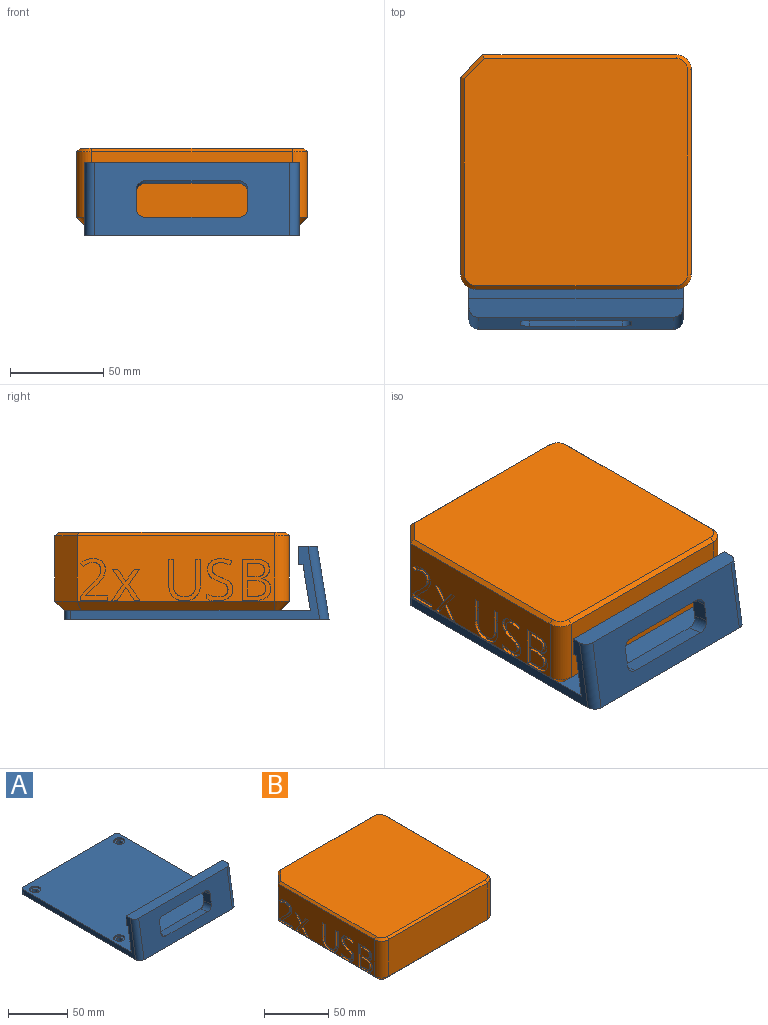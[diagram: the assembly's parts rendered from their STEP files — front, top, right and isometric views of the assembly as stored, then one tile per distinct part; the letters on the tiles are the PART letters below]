
ASSEMBLY  parts=2 mates=1
PART A: 34 faces, bbox 115x142x41.1 mm
  f0: plane 115x24.41mm, normal (0,0.99,-0.16), area 1665.7mm2, adj f4,f5,f8,f9,f22,f23,f24,f25
  f1: plane 105x39.49mm, normal (0,-0.99,0.16), area 3022.2mm2, adj f2,f7,f22,f23,f24,f25,f26,f27
  f2: plane 142x115mm, normal (0,0,-1), area 16234.2mm2, adj f1,f3,f8,f9,f10,f13,f16,f19
  f3: plane 109x5.08mm, normal (0,1,0), area 553.7mm2, adj f2,f4,f30,f31
  f4: plane 131.92x115mm, normal (0,0,1), area 14882.1mm2, adj f0,f3,f8,f9,f12,f15,f18,f21
  f5: plane 115x2.35mm, normal (0,0,-1), area 269.8mm2, adj f0,f6,f8,f9
  f6: plane 115x10mm, normal (0,1,0), area 1150mm2, adj f5,f7,f8,f9
  f7: plane 115x10mm, normal (0,0,1), area 1139.1mm2, adj f1,f6,f8,f9,f32,f33
  f8: plane 133.94x39.49mm, normal (1,0,0), area 838.2mm2, adj f0,f2,f4,f5,f6,f7,f31,f33
  f9: plane 133.94x39.49mm, normal (-1,0,0), area 838.2mm2, adj f0,f2,f4,f5,f6,f7,f30,f32
  f10: cylinder r=2.54mm len=5.08mm, axis (0,0,1), area 56.8mm2, adj f2,f11
  f11: plane 9.53x9.53mm, normal (0,0,1), area 51mm2, adj f10,f12
  f12: cylinder r=4.76mm len=9.53mm, axis (0,0,1), area 45.6mm2, adj f4,f11
  f13: cylinder r=2.54mm len=5.08mm, axis (0,0,1), area 56.8mm2, adj f2,f14
  f14: plane 9.53x9.53mm, normal (0,0,1), area 51mm2, adj f13,f15
  f15: cylinder r=4.76mm len=9.53mm, axis (0,0,1), area 45.6mm2, adj f4,f14
  f16: cylinder r=2.54mm len=5.08mm, axis (0,0,1), area 56.8mm2, adj f2,f17
  f17: plane 9.53x9.53mm, normal (0,0,1), area 51mm2, adj f16,f18
  f18: cylinder r=4.76mm len=9.53mm, axis (0,0,1), area 45.6mm2, adj f4,f17
  f19: cylinder r=2.54mm len=5.08mm, axis (0,0,1), area 56.8mm2, adj f2,f20
  f20: plane 9.53x9.53mm, normal (0,0,1), area 51mm2, adj f19,f21
  f21: cylinder r=4.76mm len=9.53mm, axis (0,0,1), area 45.6mm2, adj f4,f20
  f22: plane 11.17x10.59mm, normal (-1,0,0), area 90mm2, adj f0,f1,f26,f29
  f23: plane 49.84x9.03mm, normal (0,-0.16,-0.99), area 455.7mm2, adj f0,f1,f26,f27
  f24: plane 11.17x10.59mm, normal (1,0,0), area 90mm2, adj f0,f1,f27,f28
  f25: plane 49.84x9.03mm, normal (0,0.16,0.99), area 455.7mm2, adj f0,f1,f28,f29
  f26: cylinder r=5.08mm len=9.83mm, axis (0,-0.99,0.16), area 73mm2, adj f0,f1,f22,f23
  f27: cylinder r=5.08mm len=9.83mm, axis (0,0.99,-0.16), area 73mm2, adj f0,f1,f23,f24
  f28: cylinder r=5.08mm len=9.83mm, axis (0,-0.99,0.16), area 73mm2, adj f0,f1,f24,f25
  f29: cylinder r=5.08mm len=9.83mm, axis (0,0.99,-0.16), area 73mm2, adj f0,f1,f22,f25
  f30: cylinder r=3mm len=5.08mm, axis (0,0,1), area 23.9mm2, adj f2,f3,f4,f9
  f31: cylinder r=3mm len=5.08mm, axis (0,0,-1), area 23.9mm2, adj f2,f3,f4,f8
  f32: cylinder r=5mm len=41.08mm, axis (0,-0.16,-0.99), area 314.2mm2, adj f1,f2,f7,f9
  f33: cylinder r=5mm len=41.08mm, axis (0,0.16,0.99), area 314.2mm2, adj f1,f2,f7,f8
PART B: 268 faces, bbox 124x126x46.3 mm
  f0: plane 110x35mm, normal (1,0,0), area 3184.7mm2, adj f6,f8,f10,f121,f122,f123,f124,f125
  f1: plane 106x35mm, normal (-1,0,0), area 2969.8mm2, adj f7,f9,f17,f18,f19,f20,f27,f28
  f2: plane 104x35mm, normal (0,1,0), area 3640mm2, adj f6,f9,f13,f263
  f3: plane 108x35mm, normal (0,-1,0), area 3780mm2, adj f7,f8,f14,f264
  f4: plane 122x120mm, normal (0,0,1), area 14558.2mm2, adj f260,f261,f262,f263,f264,f265,f266,f267
  f5: plane 116x114mm, normal (0,0,-1), area 13152.7mm2, adj f10,f11,f12,f13,f14,f15,f16,f17
  f6: cylinder r=8mm len=35mm, axis (0,0,1), area 439.8mm2, adj f0,f2,f11,f261
  f7: cylinder r=8mm len=35mm, axis (0,0,1), area 439.8mm2, adj f1,f3,f16,f266
  f8: cylinder r=8mm len=35mm, axis (0,0,-1), area 439.8mm2, adj f0,f3,f12,f262
  f9: plane 35x12mm, normal (-0.71,0.71,0), area 594mm2, adj f1,f2,f15,f265
  f10: plane 110x5mm, normal (0.71,0,-0.71), area 777.8mm2, adj f0,f5,f11,f12
  f11: cone r=3mm half-angle=45deg, axis (0,0,1), area 61.1mm2, adj f5,f6,f10,f13
  f12: cone r=3mm half-angle=45deg, axis (0,0,1), area 61.1mm2, adj f5,f8,f10,f14
  f13: plane 104x5mm, normal (0,0.71,-0.71), area 728.1mm2, adj f2,f5,f11,f15
  f14: plane 108x5mm, normal (0,-0.71,-0.71), area 763.7mm2, adj f3,f5,f12,f16
  f15: plane 14.07x14.07mm, normal (-0.5,0.5,-0.71), area 105.4mm2, adj f5,f9,f13,f17
  f16: cone r=3mm half-angle=45deg, axis (0,0,1), area 61.1mm2, adj f5,f7,f14,f17
  f17: plane 106x5mm, normal (-0.71,0,-0.71), area 742.2mm2, adj f1,f5,f15,f16
  f18: plane 1.52x0.15mm, normal (0,1,0), area 0.2mm2, adj f1,f30,f31,f43
  f19: plane 6.25x1.52mm, normal (0,0,-1), area 9.5mm2, adj f1,f20,f34,f43
  f20: plane 22.11x1.52mm, normal (0,-1,0), area 33.7mm2, adj f1,f19,f27,f43
  f21: plane 4.23x1.52mm, normal (0,0,-1), area 6.5mm2, adj f22,f38,f43,f44
  f22: plane 7.24x1.52mm, normal (0,1,0), area 11mm2, adj f21,f26,f43,f44
  f23: plane 4.62x1.52mm, normal (0,0,-1), area 7mm2, adj f24,f41,f43,f45
  f24: plane 8.27x1.52mm, normal (0,1,0), area 12.6mm2, adj f23,f25,f43,f45
  f25: plane 4.4x1.52mm, normal (0,0,1), area 6.7mm2, adj f24,f42,f43,f45
  f26: plane 3.78x1.52mm, normal (0,0,1), area 5.8mm2, adj f22,f35,f43,f44
  f27: plane 7.71x1.52mm, normal (0,0,1), area 11.8mm2, adj f1,f20,f28,f43
  f28: extruded ~5.6x1.66mm, area 9.1mm2, adj f1,f27,f29,f43
  f29: extruded ~4.63x2mm, area 8mm2, adj f1,f28,f30,f43
  f30: extruded ~5.29x5.04mm, area 12.3mm2, adj f1,f18,f29,f43
  f31: extruded ~3.2x1.66mm, area 5.6mm2, adj f1,f18,f32,f43
  f32: extruded ~3.25x1.52mm, area 5.3mm2, adj f1,f31,f33,f43
  f33: extruded ~4.16x1.97mm, area 7.3mm2, adj f1,f32,f34,f43
  f34: extruded ~6.37x1.52mm, area 10mm2, adj f1,f19,f33,f43
  f35: extruded ~4.23x1.52mm, area 6.6mm2, adj f26,f36,f43,f44
  f36: extruded ~2.69x1.52mm, area 4.8mm2, adj f35,f37,f43,f44
  f37: extruded ~2.88x1.52mm, area 4.9mm2, adj f36,f38,f43,f44
  f38: extruded ~3.92x1.52mm, area 6.2mm2, adj f21,f37,f43,f44
  f39: extruded ~3.02x1.52mm, area 5.3mm2, adj f40,f42,f43,f45
  f40: extruded ~3.25x1.52mm, area 5.6mm2, adj f39,f41,f43,f45
  f41: extruded ~4.03x1.52mm, area 6.4mm2, adj f23,f40,f43,f45
  f42: extruded ~4.21x1.52mm, area 6.7mm2, adj f25,f39,f43,f45
  f43: plane 22.11x15.32mm, normal (-1,0,0), area 166.7mm2, adj f18,f19,f20,f21,f22,f23,f24,f25
  f44: plane 9.35x7.24mm, normal (-1,0,0), area 61.8mm2, adj f21,f22,f26,f35,f36,f37,f38
  f45: plane 10x8.27mm, normal (-1,0,0), area 75.4mm2, adj f23,f24,f25,f39,f40,f41,f42
  f46: plane 2.24x1.52mm, normal (0,0.94,0.34), area 3.6mm2, adj f1,f53,f54,f71
  f47: plane 2.48x1.52mm, normal (0,-1,0), area 3.8mm2, adj f1,f65,f66,f71
  f48: extruded ~3.08x1.52mm, area 5.1mm2, adj f1,f49,f70,f71
  f49: extruded ~1.52x1.43mm, area 3mm2, adj f1,f48,f50,f71
  f50: extruded ~1.88x1.52mm, area 3mm2, adj f1,f49,f51,f71
  f51: extruded ~2.43x1.52mm, area 4.3mm2, adj f1,f50,f52,f71
  f52: extruded ~3.19x1.52mm, area 5.1mm2, adj f1,f51,f53,f71
  f53: extruded ~5.32x1.52mm, area 8.4mm2, adj f1,f46,f52,f71
  f54: extruded ~6.06x1.52mm, area 9.5mm2, adj f1,f46,f55,f71
  f55: extruded ~5.08x1.52mm, area 8.2mm2, adj f1,f54,f56,f71
  f56: extruded ~4.07x1.92mm, area 7.1mm2, adj f1,f55,f57,f71
  f57: extruded ~3.95x1.52mm, area 6.5mm2, adj f1,f56,f58,f71
  f58: extruded ~4.41x2.62mm, area 7.9mm2, adj f1,f57,f59,f71
  f59: extruded ~3.29x1.52mm, area 5.5mm2, adj f1,f58,f60,f71
  f60: extruded ~1.54x1.52mm, area 3.2mm2, adj f1,f59,f61,f71
  f61: extruded ~1.88x1.52mm, area 3mm2, adj f1,f60,f62,f71
  f62: extruded ~2.72x1.52mm, area 4.8mm2, adj f1,f61,f63,f71
  f63: extruded ~3.87x1.52mm, area 6.2mm2, adj f1,f62,f64,f71
  f64: extruded ~3.17x1.52mm, area 4.9mm2, adj f1,f63,f65,f71
  f65: extruded ~2.97x1.52mm, area 4.7mm2, adj f1,f47,f64,f71
  f66: extruded ~6.05x1.52mm, area 9.4mm2, adj f1,f47,f67,f71
  f67: extruded ~5.75x1.64mm, area 9.3mm2, adj f1,f66,f68,f71
  f68: extruded ~4.55x2.12mm, area 7.9mm2, adj f1,f67,f69,f71
  f69: extruded ~3.69x1.52mm, area 6.1mm2, adj f1,f68,f70,f71
  f70: extruded ~4.79x2.66mm, area 8.4mm2, adj f1,f48,f69,f71
  f71: plane 22.73x13.91mm, normal (-1,0,0), area 113.1mm2, adj f46,f47,f48,f49,f50,f51,f52,f53
  f72: plane 14.42x1.52mm, normal (0,1,0), area 22mm2, adj f1,f73,f81,f86
  f73: plane 2.57x1.52mm, normal (0,0,-1), area 3.9mm2, adj f1,f72,f74,f86
  f74: plane 14.25x1.52mm, normal (0,-1,0), area 21.7mm2, adj f1,f73,f82,f86
  f75: plane 14.3x1.52mm, normal (0,1,0), area 21.8mm2, adj f1,f76,f85,f86
  f76: plane 2.57x1.52mm, normal (0,0,-1), area 3.9mm2, adj f1,f75,f77,f86
  f77: plane 14.4x1.52mm, normal (0,-1,0), area 21.9mm2, adj f1,f76,f78,f86
  f78: extruded ~4.27x1.52mm, area 7.1mm2, adj f1,f77,f79,f86
  f79: extruded ~4.31x1.52mm, area 7.1mm2, adj f1,f78,f80,f86
  f80: extruded ~4.44x1.52mm, area 7.3mm2, adj f1,f79,f81,f86
  f81: extruded ~4.25x1.52mm, area 7.1mm2, adj f1,f72,f80,f86
  f82: extruded ~5.99x2.18mm, area 10mm2, adj f1,f74,f83,f86
  f83: extruded ~6.18x2.18mm, area 10.3mm2, adj f1,f82,f84,f86
  f84: extruded ~6.28x2.16mm, area 10.4mm2, adj f1,f83,f85,f86
  f85: extruded ~5.95x2.28mm, area 10mm2, adj f1,f75,f84,f86
  f86: plane 22.41x16.92mm, normal (-1,0,0), area 128.5mm2, adj f72,f73,f74,f75,f76,f77,f78,f79
  f87: plane 6.72x4.69mm, normal (0,0.82,0.57), area 12.5mm2, adj f1,f88,f98,f99
  f88: plane 6.72x4.65mm, normal (0,-0.82,0.57), area 12.4mm2, adj f1,f87,f89,f99
  f89: plane 2.84x1.52mm, normal (0,0,1), area 4.3mm2, adj f1,f88,f90,f99
  f90: plane 8.48x6.06mm, normal (0,0.81,-0.58), area 15.9mm2, adj f1,f89,f91,f99
  f91: plane 8.09x5.76mm, normal (0,0.81,0.58), area 15.1mm2, adj f1,f90,f92,f99
  f92: plane 2.83x1.52mm, normal (0,0,-1), area 4.3mm2, adj f1,f91,f93,f99
  f93: plane 6.35x4.36mm, normal (0,-0.82,-0.57), area 11.7mm2, adj f1,f92,f94,f99
  f94: plane 6.35x4.37mm, normal (0,0.82,-0.57), area 11.7mm2, adj f1,f93,f95,f99
  f95: plane 2.86x1.52mm, normal (0,0,-1), area 4.4mm2, adj f1,f94,f96,f99
  f96: plane 8.09x5.76mm, normal (0,-0.81,0.58), area 15.1mm2, adj f1,f95,f97,f99
  f97: plane 8.48x6.06mm, normal (0,-0.81,-0.58), area 15.9mm2, adj f1,f96,f98,f99
  f98: plane 2.84x1.52mm, normal (0,0,1), area 4.3mm2, adj f1,f87,f97,f99
  f99: plane 16.57x15.02mm, normal (-1,0,0), area 86.9mm2, adj f87,f88,f89,f90,f91,f92,f93,f94
  f100: plane 1.52x0.12mm, normal (0,1,0), area 0.2mm2, adj f1,f101,f107,f120
  f101: plane 4.84x4.73mm, normal (0,0.7,0.71), area 10.3mm2, adj f1,f100,f108,f120
  f102: plane 1.71x1.52mm, normal (0,-0.79,0.61), area 3.3mm2, adj f1,f112,f113,f120
  f103: plane 5.85x5.82mm, normal (0,-0.71,-0.71), area 12.6mm2, adj f1,f104,f119,f120
  f104: plane 2.16x1.52mm, normal (0,-1,0), area 3.3mm2, adj f1,f103,f105,f120
  f105: plane 14.53x1.52mm, normal (0,0,1), area 22.1mm2, adj f1,f104,f106,f120
  f106: plane 2.33x1.52mm, normal (0,1,0), area 3.5mm2, adj f1,f105,f107,f120
  f107: plane 11.37x1.52mm, normal (0,0,-1), area 17.3mm2, adj f1,f100,f106,f120
  f108: extruded ~5.2x4.41mm, area 10.4mm2, adj f1,f101,f109,f120
  f109: extruded ~4.16x1.52mm, area 6.7mm2, adj f1,f108,f110,f120
  f110: extruded ~4.29x1.77mm, area 7.3mm2, adj f1,f109,f111,f120
  f111: extruded ~4.89x1.59mm, area 8mm2, adj f1,f110,f112,f120
  f112: extruded ~6.65x2.54mm, area 11.1mm2, adj f1,f102,f111,f120
  f113: extruded ~2.74x1.65mm, area 4.9mm2, adj f1,f102,f114,f120
  f114: extruded ~2.61x1.52mm, area 4.1mm2, adj f1,f113,f115,f120
  f115: extruded ~2.98x1.52mm, area 4.9mm2, adj f1,f114,f116,f120
  f116: extruded ~2.81x1.52mm, area 4.7mm2, adj f1,f115,f117,f120
  f117: extruded ~2.34x1.52mm, area 3.6mm2, adj f1,f116,f118,f120
  f118: extruded ~2.24x1.52mm, area 3.9mm2, adj f1,f117,f119,f120
  f119: extruded ~3.84x3.51mm, area 7.9mm2, adj f1,f103,f118,f120
  f120: plane 22.42x14.53mm, normal (-1,0,0), area 107.7mm2, adj f100,f101,f102,f103,f104,f105,f106,f107
  f121: extruded ~2.95x1.52mm, area 4.9mm2, adj f0,f122,f132,f134
  f122: extruded ~2.49x1.52mm, area 4.3mm2, adj f0,f121,f123,f134
  f123: extruded ~1.52x1.32mm, area 2mm2, adj f0,f122,f133,f134
  f124: extruded ~1.52x1.43mm, area 2.2mm2, adj f0,f125,f133,f134
  f125: extruded ~2.07x1.52mm, area 3.4mm2, adj f0,f124,f126,f134
  f126: extruded ~1.81x1.61mm, area 3.7mm2, adj f0,f125,f127,f134
  f127: plane 1.52x0.09mm, normal (0,0,-1), area 0.1mm2, adj f0,f126,f128,f134
  f128: plane 2.22x1.52mm, normal (0,-1,-0.09), area 3.4mm2, adj f0,f127,f129,f134
  f129: plane 1.52x1.5mm, normal (0,0,-1), area 2.3mm2, adj f0,f128,f130,f134
  f130: plane 12.01x1.52mm, normal (0,1,0), area 18.3mm2, adj f0,f129,f131,f134
  f131: plane 1.82x1.52mm, normal (0,0,1), area 2.8mm2, adj f0,f130,f132,f134
  f132: plane 6.44x1.52mm, normal (0,-1,0), area 9.8mm2, adj f0,f121,f131,f134
  f133: plane 1.69x1.52mm, normal (0,-0.99,0.15), area 2.6mm2, adj f0,f123,f124,f134
  f134: plane 12.23x6.91mm, normal (1,0,0), area 30.1mm2, adj f121,f122,f123,f124,f125,f126,f127,f128
  f135: extruded ~3.83x1.52mm, area 6mm2, adj f0,f136,f150,f154
  f136: extruded ~2.85x1.52mm, area 4.8mm2, adj f0,f135,f137,f154
  f137: extruded ~3.21x1.52mm, area 5.3mm2, adj f0,f136,f151,f154
  f138: extruded ~3.92x1.52mm, area 6.4mm2, adj f0,f139,f152,f154
  f139: extruded ~3.57x1.52mm, area 6.1mm2, adj f0,f138,f140,f154
  f140: extruded ~3.84x1.71mm, area 6.6mm2, adj f0,f139,f141,f154
  f141: extruded ~4.62x1.52mm, area 7.5mm2, adj f0,f140,f142,f154
  f142: extruded ~4.5x1.54mm, area 7.4mm2, adj f0,f141,f143,f154
  f143: extruded ~4.2x1.62mm, area 7.1mm2, adj f0,f142,f144,f154
  f144: extruded ~2.08x1.52mm, area 3.2mm2, adj f0,f143,f149,f154
  f145: extruded ~2.61x1.52mm, area 4.3mm2, adj f146,f153,f154,f155
  f146: extruded ~2.31x1.52mm, area 3.9mm2, adj f145,f147,f154,f155
  f147: extruded ~2.19x1.52mm, area 3.7mm2, adj f146,f148,f154,f155
  f148: extruded ~2.63x1.52mm, area 4.3mm2, adj f147,f153,f154,f155
  f149: extruded ~1.82x1.52mm, area 2.9mm2, adj f0,f144,f150,f154
  f150: plane 1.62x1.52mm, normal (0,-1,0), area 2.5mm2, adj f0,f135,f149,f154
  f151: plane 8.27x1.52mm, normal (0,0,1), area 12.6mm2, adj f0,f137,f152,f154
  f152: plane 1.52x1.15mm, normal (0,-1,0), area 1.8mm2, adj f0,f138,f151,f154
  f153: plane 6.28x1.52mm, normal (0,0,-1), area 9.6mm2, adj f145,f148,f154,f155
  f154: plane 12.45x10.16mm, normal (1,0,0), area 57.5mm2, adj f135,f136,f137,f138,f139,f140,f141,f142
  f155: plane 6.28x3.55mm, normal (1,0,0), area 18mm2, adj f145,f146,f147,f148,f153
  f156: extruded ~8.84x2.28mm, area 13.9mm2, adj f0,f157,f165,f179
  f157: extruded ~1.52x1.22mm, area 1.9mm2, adj f0,f156,f166,f179
  f158: extruded ~3.17x1.52mm, area 5mm2, adj f0,f166,f167,f179
  f159: extruded ~1.57x1.52mm, area 2.5mm2, adj f0,f160,f169,f179
  f160: extruded ~1.62x1.52mm, area 2.5mm2, adj f0,f159,f170,f179
  f161: extruded ~3.19x1.52mm, area 5mm2, adj f0,f162,f170,f179
  f162: extruded ~6.89x1.77mm, area 10.8mm2, adj f0,f161,f171,f179
  f163: extruded ~2.96x1.52mm, area 4.7mm2, adj f0,f174,f175,f179
  f164: extruded ~2.94x1.52mm, area 4.6mm2, adj f0,f175,f176,f179
  f165: plane 1.88x1.52mm, normal (0,0,-1), area 2.9mm2, adj f0,f156,f178,f179
  f166: plane 1.52x0.09mm, normal (0,0,-1), area 0.1mm2, adj f0,f157,f158,f179
  f167: plane 6.89x2.15mm, normal (0,-0.95,-0.3), area 11mm2, adj f0,f158,f168,f179
  f168: plane 1.97x1.52mm, normal (0,0,-1), area 3mm2, adj f0,f167,f169,f179
  f169: plane 6.89x2.2mm, normal (0,0.95,-0.3), area 11mm2, adj f0,f159,f168,f179
  f170: plane 1.52x0.09mm, normal (0,0,-1), area 0.1mm2, adj f0,f160,f161,f179
  f171: plane 1.91x1.52mm, normal (0,0,-1), area 2.9mm2, adj f0,f162,f172,f179
  f172: plane 12.01x3.28mm, normal (0,0.96,0.26), area 19mm2, adj f0,f171,f173,f179
  f173: plane 2.1x1.52mm, normal (0,0,1), area 3.2mm2, adj f0,f172,f174,f179
  f174: plane 7.02x2.27mm, normal (0,-0.95,0.31), area 11.2mm2, adj f0,f163,f173,f179
  f175: plane 1.52x0.09mm, normal (0,0,1), area 0.1mm2, adj f0,f163,f164,f179
  f176: plane 7.04x2.2mm, normal (0,0.95,0.3), area 11.2mm2, adj f0,f164,f177,f179
  f177: plane 2.16x1.52mm, normal (0,0,1), area 3.3mm2, adj f0,f176,f178,f179
  f178: plane 12.01x3.32mm, normal (0,-0.96,0.27), area 19mm2, adj f0,f165,f177,f179
  f179: plane 16.96x12.01mm, normal (1,0,0), area 79.4mm2, adj f156,f157,f158,f159,f160,f161,f162,f163
  f180: extruded ~4.08x1.64mm, area 6.9mm2, adj f0,f181,f196,f197
  f181: extruded ~4.57x1.52mm, area 7.5mm2, adj f0,f180,f182,f197
  f182: extruded ~3.31x1.52mm, area 5.2mm2, adj f0,f181,f183,f197
  f183: extruded ~2.17x1.93mm, area 4.5mm2, adj f0,f182,f184,f197
  f184: extruded ~2.86x1.52mm, area 4.6mm2, adj f0,f183,f185,f197
  f185: extruded ~4.09x1.65mm, area 6.9mm2, adj f0,f184,f186,f197
  f186: extruded ~4.59x1.52mm, area 7.5mm2, adj f0,f185,f187,f197
  f187: extruded ~4.54x1.52mm, area 7.4mm2, adj f0,f186,f196,f197
  f188: extruded ~2.74x1.52mm, area 4.7mm2, adj f189,f195,f197,f198
  f189: extruded ~3.48x1.52mm, area 5.6mm2, adj f188,f190,f197,f198
  f190: extruded ~3.51x1.52mm, area 5.6mm2, adj f189,f191,f197,f198
  f191: extruded ~2.71x1.52mm, area 4.7mm2, adj f190,f192,f197,f198
  f192: extruded ~2.71x1.52mm, area 4.7mm2, adj f191,f193,f197,f198
  f193: extruded ~3.51x1.52mm, area 5.6mm2, adj f192,f194,f197,f198
  f194: extruded ~3.49x1.52mm, area 5.6mm2, adj f193,f195,f197,f198
  f195: extruded ~2.69x1.52mm, area 4.6mm2, adj f188,f194,f197,f198
  f196: extruded ~4x1.68mm, area 6.8mm2, adj f0,f180,f187,f197
  f197: plane 12.45x11.03mm, normal (1,0,0), area 55.4mm2, adj f180,f181,f182,f183,f184,f185,f186,f187
  f198: plane 9.38x7.27mm, normal (1,0,0), area 56.5mm2, adj f188,f189,f190,f191,f192,f193,f194,f195
  f199: extruded ~4.75x1.52mm, area 7.6mm2, adj f0,f200,f209,f214
  f200: extruded ~3.74x1.66mm, area 6.5mm2, adj f0,f199,f201,f214
  f201: extruded ~6x4.67mm, area 13.2mm2, adj f0,f200,f213,f214
  f202: extruded ~3.24x1.52mm, area 5.2mm2, adj f203,f212,f214,f215
  f203: extruded ~2.37x1.52mm, area 4.1mm2, adj f202,f204,f214,f215
  f204: extruded ~2.57x1.52mm, area 4.4mm2, adj f203,f205,f214,f215
  f205: extruded ~3.58x1.52mm, area 5.7mm2, adj f204,f210,f214,f215
  f206: plane 16.02x1.52mm, normal (0,1,0), area 24.4mm2, adj f0,f207,f213,f214
  f207: plane 1.86x1.52mm, normal (0,0,1), area 2.8mm2, adj f0,f206,f208,f214
  f208: plane 6.3x1.52mm, normal (0,-1,0), area 9.6mm2, adj f0,f207,f209,f214
  f209: plane 1.89x1.52mm, normal (0,0,1), area 2.9mm2, adj f0,f199,f208,f214
  f210: plane 1.68x1.52mm, normal (0,0,-1), area 2.6mm2, adj f205,f211,f214,f215
  f211: plane 6.51x1.52mm, normal (0,-1,0), area 9.9mm2, adj f210,f212,f214,f215
  f212: plane 2.08x1.52mm, normal (0,0,1), area 3.2mm2, adj f202,f211,f214,f215
  f213: plane 4.16x1.52mm, normal (0,0,-1), area 6.3mm2, adj f0,f201,f206,f214
  f214: plane 16.02x10.16mm, normal (1,0,0), area 63.3mm2, adj f199,f200,f201,f202,f203,f204,f205,f206
  f215: plane 6.51x6.37mm, normal (1,0,0), area 36.8mm2, adj f202,f203,f204,f205,f210,f211,f212
  f216: extruded ~2.82x1.52mm, area 4.4mm2, adj f0,f219,f220,f223
  f217: extruded ~2.7x1.52mm, area 4.5mm2, adj f0,f218,f220,f223
  f218: extruded ~2.55x1.52mm, area 4.1mm2, adj f0,f217,f221,f223
  f219: extruded ~2.69x1.52mm, area 4.2mm2, adj f0,f216,f222,f223
  f220: plane 1.52x1.37mm, normal (0,0,1), area 2.1mm2, adj f0,f216,f217,f223
  f221: plane 1.52x0.25mm, normal (0,-0.84,-0.55), area 0.5mm2, adj f0,f218,f222,f223
  f222: plane 2x1.52mm, normal (0,0,-1), area 3mm2, adj f0,f219,f221,f223
  f223: plane 5.5x3.31mm, normal (1,0,0), area 10.1mm2, adj f216,f217,f218,f219,f220,f221,f222
  f224: extruded ~5.48x2.15mm, area 9.3mm2, adj f0,f225,f239,f240
  f225: extruded ~6.07x1.93mm, area 9.9mm2, adj f0,f224,f226,f240
  f226: extruded ~6.11x1.92mm, area 10mm2, adj f0,f225,f227,f240
  f227: extruded ~5.46x2.17mm, area 9.2mm2, adj f0,f226,f228,f240
  f228: extruded ~5.41x2.2mm, area 9.2mm2, adj f0,f227,f229,f240
  f229: extruded ~6.05x1.95mm, area 9.9mm2, adj f0,f228,f230,f240
  f230: extruded ~6.05x1.94mm, area 9.9mm2, adj f0,f229,f239,f240
  f231: extruded ~4x1.67mm, area 6.9mm2, adj f232,f238,f240,f241
  f232: extruded ~4.9x1.52mm, area 7.9mm2, adj f231,f233,f240,f241
  f233: extruded ~4.94x1.52mm, area 8mm2, adj f232,f234,f240,f241
  f234: extruded ~4.02x1.68mm, area 6.9mm2, adj f233,f235,f240,f241
  f235: extruded ~4.03x1.68mm, area 6.9mm2, adj f234,f236,f240,f241
  f236: extruded ~4.94x1.52mm, area 8mm2, adj f235,f237,f240,f241
  f237: extruded ~4.89x1.52mm, area 7.9mm2, adj f236,f238,f240,f241
  f238: extruded ~4.05x1.68mm, area 6.9mm2, adj f231,f237,f240,f241
  f239: extruded ~5.39x2.19mm, area 9.2mm2, adj f0,f224,f230,f240
  f240: plane 16.49x14.74mm, normal (1,0,0), area 81.2mm2, adj f224,f225,f226,f227,f228,f229,f230,f231
  f241: plane 13.19x10.79mm, normal (1,0,0), area 118.1mm2, adj f231,f232,f233,f234,f235,f236,f237,f238
  f242: plane 1.82x1.52mm, normal (0,0,1), area 2.8mm2, adj f0,f243,f245,f246
  f243: plane 16.02x5.97mm, normal (0,-0.94,0.35), area 26.1mm2, adj f0,f242,f244,f246
  f244: plane 1.82x1.52mm, normal (0,0,-1), area 2.8mm2, adj f0,f243,f245,f246
  f245: plane 16.02x5.97mm, normal (0,0.94,-0.35), area 26.1mm2, adj f0,f242,f244,f246
  f246: plane 16.02x7.79mm, normal (1,0,0), area 29.1mm2, adj f242,f243,f244,f245
  f247: plane 1.86x1.52mm, normal (0,0,-1), area 2.8mm2, adj f0,f248,f250,f251
  f248: plane 16.02x1.52mm, normal (0,1,0), area 24.4mm2, adj f0,f247,f249,f251
  f249: plane 1.86x1.52mm, normal (0,0,1), area 2.8mm2, adj f0,f248,f250,f251
  f250: plane 16.02x1.52mm, normal (0,-1,0), area 24.4mm2, adj f0,f247,f249,f251
  f251: plane 16.02x1.86mm, normal (1,0,0), area 29.8mm2, adj f247,f248,f249,f250
  f252: cylinder r=1.97mm len=3.94mm, axis (0,0,1), area 43.3mm2, adj f5,f256
  f253: cylinder r=1.97mm len=3.94mm, axis (0,0,1), area 43.3mm2, adj f5,f259
  f254: cylinder r=4mm len=8mm, axis (0,0,1), area 19.2mm2, adj f255,f256
  f255: plane 8x8mm, normal (0,0,-1), area 50.3mm2, adj f254
  f256: plane 8x8mm, normal (0,0,1), area 38.1mm2, adj f252,f254
  f257: cylinder r=4mm len=8mm, axis (0,0,1), area 19.2mm2, adj f258,f259
  f258: plane 8x8mm, normal (0,0,-1), area 50.3mm2, adj f257
  f259: plane 8x8mm, normal (0,0,1), area 38.1mm2, adj f253,f257
  f260: plane 110x2mm, normal (0.71,0,0.71), area 311.1mm2, adj f0,f4,f261,f262
  f261: cone r=6mm half-angle=45deg, axis (0,0,-1), area 31.1mm2, adj f4,f6,f260,f263
  f262: cone r=6mm half-angle=45deg, axis (0,0,-1), area 31.1mm2, adj f4,f8,f260,f264
  f263: plane 104x2mm, normal (0,0.71,0.71), area 293mm2, adj f2,f4,f261,f265
  f264: plane 108x2mm, normal (0,-0.71,0.71), area 305.5mm2, adj f3,f4,f262,f266
  f265: plane 12.83x12.83mm, normal (-0.5,0.5,0.71), area 45.7mm2, adj f4,f9,f263,f267
  f266: cone r=6mm half-angle=45deg, axis (0,0,-1), area 31.1mm2, adj f4,f7,f264,f267
  f267: plane 106x2mm, normal (-0.71,0,0.71), area 298.6mm2, adj f1,f4,f265,f266
PLACE A t=(0,-29.34,-5.08)mm
PLACE B t=(0,-16,0)mm
MATE fastened B.f5 <-> A.f4  axis (0,0,-1) through (0,0,0)mm
